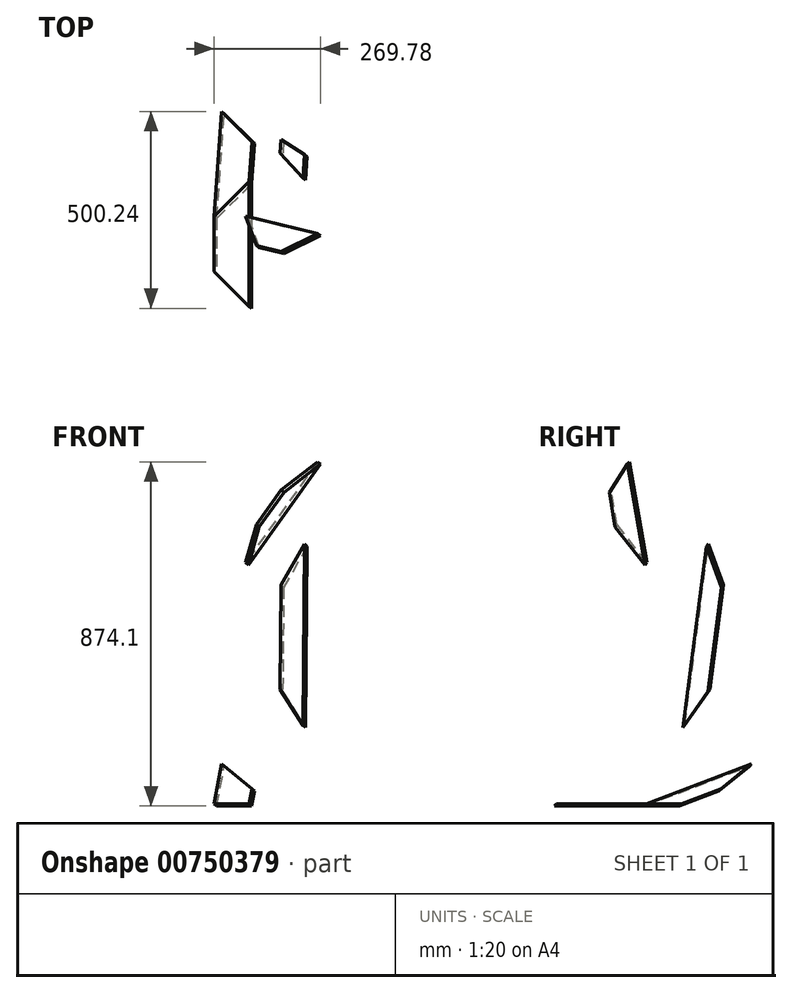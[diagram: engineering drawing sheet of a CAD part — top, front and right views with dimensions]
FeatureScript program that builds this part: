
annotation { "Feature Type Name" : "Feature", "Feature Type Description" : "" }
export const myFeature = defineFeature(function(context is Context, id is Id, definition is map)
    precondition{}
    {
        {
            var Q0;
            Q0=qCreatedBy(makeId("Top.planeOp"),FACE);
            var sketch = newSketch(context, id + "F0", { "sketchPlane" : qUnion([Q0])});
            skLineSegment(sketch, "E0", {"start": v(0, -158.75) * mm, "end": v(0, 158.75) * mm, "construction": true});
            skLineSegment(sketch, "E1", {"start": v(-44.45, 158.75) * mm, "end": v(44.45, 158.75) * mm, "construction": true});
            skLineSegment(sketch, "E2", {"start": v(-44.45, 0) * mm, "end": v(44.45, 0) * mm});
            skLineSegment(sketch, "E3", {"start": v(44.45, 0) * mm, "end": v(44.45, 158.75) * mm});
            skLineSegment(sketch, "E4", {"start": v(-44.45, 0) * mm, "end": v(-44.45, 69.85) * mm});
            skLineSegment(sketch, "E5", {"start": v(-44.45, 69.85) * mm, "end": v(44.45, 158.75) * mm});
            skLineSegment(sketch, "E6.MirrorCS", {"start": v(-44.45, 0) * mm, "end": v(-44.45, -69.85) * mm});
            skLineSegment(sketch, "E7.MirrorCS", {"start": v(-44.45, -69.85) * mm, "end": v(44.45, -158.75) * mm});
            skLineSegment(sketch, "E8.MirrorCS", {"start": v(44.45, 0) * mm, "end": v(44.45, -158.75) * mm});
            skLineSegment(sketch, "E9", {"start": v(44.45, 69.85) * mm, "end": v(-77.04, 191.34) * mm, "construction": true});
            skPoint(sketch, "E10", {"position": v(0, 114.3) * mm});
            skLineSegment(sketch, "E11.MirrorCS", {"start": v(44.45, -69.85) * mm, "end": v(-77.04, -191.34) * mm, "construction": true});
            skPoint(sketch, "E12.MirrorP", {"position": v(0, -114.3) * mm});
            skSolve(sketch);
        }
        {
            var Q0;
            Q0=sQuery(id+"F0.wireOp",VERTEX,"E10");
            var Q1;
            Q1=sQuery(id+"F0.wireOp",EDGE,"E5");
            cPlane(context, id + "F1", {"entities" : qUnion([Q0, Q1]), "cplaneType" : CPlaneType.LINE_POINT, "offset" : 25.4 * mm, "width" : 152.4 * mm, "height" : 152.4 * mm});
        }
        {
            assignVariable(context, id + "F2", {"name" : "al", "anyValue" : 30});
        }
        {
            var Q0;
            Q0=qCreatedBy(id+"F1.planeOp",FACE);
            var sketch = newSketch(context, id + "F3", { "sketchPlane" : qUnion([Q0])});
            skLineSegment(sketch, "E13", {"start": v(80.82, 0) * mm, "end": v(313.77, 134.5) * mm, "construction": true});
            skLineSegment(sketch, "E14", {"start": v(80.82, 0) * mm, "end": v(-55.6, 236.3) * mm, "construction": true});
            skSolve(sketch);
        }
        {
            var Q0;
            Q0=sQuery(id+"F0.wireOp",EDGE,"E5");
            cPoint(context, id + "F4", {"entities" : qUnion([Q0]), "parameter" : 0.5});
        }
        {
            var Q0;
            Q0 = qCreatedBy(id + "F4" ,VERTEX);
            var Q1;
            Q1=sQuery(id+"F3.wireOp",EDGE,"E14");
            cPlane(context, id + "F5", {"entities" : qUnion([Q0, Q1]), "cplaneType" : CPlaneType.LINE_POINT, "offset" : 25.4 * mm, "width" : 152.4 * mm, "height" : 152.4 * mm});
        }
        {
            var Q0;
            Q0=qCreatedBy(id+"F5.planeOp",FACE);
            var sketch = newSketch(context, id + "F6", { "sketchPlane" : qUnion([Q0])});
            skPoint(sketch, "E15", {"position": v(15.27, 105.82) * mm});
            skLineSegment(sketch, "E16", {"start": v(15.27, 105.82) * mm, "end": v(15.87, 114.08) * mm, "construction": true});
            skLineSegment(sketch, "E17", {"start": v(-32.25, 64.67) * mm, "end": v(-11.76, 349.97) * mm});
            skLineSegment(sketch, "E18", {"start": v(70.54, 254.94) * mm, "end": v(62.8, 146.97) * mm});
            skLineSegment(sketch, "E19", {"start": v(62.8, 146.97) * mm, "end": v(-32.25, 64.67) * mm});
            skLineSegment(sketch, "E20", {"start": v(-178.95, 218.59) * mm, "end": v(135.87, 195.99) * mm, "construction": true});
            skPoint(sketch, "E21", {"position": v(-22, 207.32) * mm});
            skLineSegment(sketch, "E22.MirrorCS", {"start": v(70.54, 254.94) * mm, "end": v(-11.76, 349.97) * mm});
            skPoint(sketch, "E23", {"position": v(66.67, 200.95) * mm});
            skLineSegment(sketch, "E24", {"start": v(-18.13, 261.3) * mm, "end": v(108.46, 370.93) * mm, "construction": true});
            skPoint(sketch, "E25", {"position": v(29.4, 302.45) * mm});
            skSolve(sketch);
        }
        {
            var Q0;
            Q0=sQuery(id+"F6.wireOp",VERTEX,"E25");
            var Q1;
            Q1=sQuery(id+"F6.wireOp",EDGE,"E22.MirrorCS");
            cPlane(context, id + "F7", {"entities" : qUnion([Q0, Q1]), "cplaneType" : CPlaneType.LINE_POINT, "offset" : 25.4 * mm, "width" : 152.4 * mm, "height" : 152.4 * mm});
        }
        {
            var Q0;
            Q0=qCreatedBy(id+"F7.planeOp",FACE);
            var sketch = newSketch(context, id + "F8", { "sketchPlane" : qUnion([Q0])});
            skLineSegment(sketch, "E26", {"start": v(-215.04, 62.34) * mm, "end": v(-136.1, 114.46) * mm, "construction": true});
            skLineSegment(sketch, "E27", {"start": v(-215.04, 62.34) * mm, "end": v(-258.43, 128.06) * mm, "construction": true});
            skSolve(sketch);
        }
        {
            var Q0;
            Q0=sQuery(id+"F8.wireOp",EDGE,"E26");
            var Q1;
            Q1=sQuery(id+"F6.wireOp",VERTEX,"E25");
            cPlane(context, id + "F9", {"entities" : qUnion([Q0, Q1]), "cplaneType" : CPlaneType.LINE_POINT, "offset" : 25.4 * mm, "width" : 152.4 * mm, "height" : 152.4 * mm});
        }
        {
            var Q0;
            Q0=qCreatedBy(id+"F9.planeOp",FACE);
            var sketch = newSketch(context, id + "F10", { "sketchPlane" : qUnion([Q0])});
            skLineSegment(sketch, "E28", {"start": v(44.88, 220.3) * mm, "end": v(50.56, 684.58) * mm});
            skLineSegment(sketch, "E29", {"start": v(50.56, 684.58) * mm, "end": v(-28.92, 587.17) * mm});
            skLineSegment(sketch, "E30", {"start": v(-28.92, 587.17) * mm, "end": v(-32.2, 319.62) * mm});
            skLineSegment(sketch, "E31", {"start": v(-32.2, 319.62) * mm, "end": v(44.88, 220.3) * mm});
            skLineSegment(sketch, "E32", {"start": v(-30.56, 453.4) * mm, "end": v(47.72, 452.44) * mm, "construction": true});
            skPoint(sketch, "E33", {"position": v(10.82, 635.87) * mm});
            skLineSegment(sketch, "E34", {"start": v(10.82, 635.87) * mm, "end": v(-66.7, 699.11) * mm, "construction": true});
            skSolve(sketch);
        }
        {
            var Q0;
            Q0=sQuery(id+"F10.wireOp",EDGE,"E29");
            cPlane(context, id + "F11", {"entities" : qUnion([Q0]), "cplaneType" : CPlaneType.LINE_ANGLE, "offset" : 25.4 * mm, "angle" : (getVariable(context, 'al')) * degree, "width" : 152.4 * mm, "height" : 152.4 * mm});
        }
        {
            var Q0;
            Q0=qCreatedBy(id+"F11.planeOp",FACE);
            var sketch = newSketch(context, id + "F12", { "sketchPlane" : qUnion([Q0])});
            skLineSegment(sketch, "E35", {"start": v(197.52, 584.55) * mm, "end": v(214.81, 691.72) * mm});
            skLineSegment(sketch, "E36", {"start": v(214.81, 691.72) * mm, "end": v(162.4, 806) * mm});
            skLineSegment(sketch, "E37", {"start": v(162.4, 806) * mm, "end": v(111.84, 492.55) * mm});
            skLineSegment(sketch, "E38", {"start": v(111.84, 492.55) * mm, "end": v(197.52, 584.55) * mm});
            skLineSegment(sketch, "E39", {"start": v(206.17, 638.13) * mm, "end": v(137.11, 649.27) * mm});
            skSolve(sketch);
        }
        {
            var Q0;
            {var subQ0=sQuery(id+"F12.wireOp",EDGE,"E38");Q0=makeQuery(id+"F12.imprint","IMPRINT",FACE,{"disambiguationData":[TD([[makeQuery(id+"F12.imprint","IMPRINT",EDGE,{"derivedFrom":subQ0}),1.0]])]});}
            var Q1;
            Q1=makeQuery(id+"F6.imprint","IMPRINT",FACE,{"disambiguationData":[TD([[makeQuery(id+"F6.imprint","IMPRINT",EDGE,{"derivedFrom":sQuery(id+"F6.wireOp",EDGE,"E17")}),-1.0]])]});
            var Q2;
            Q2=makeQuery(id+"F10.imprint","IMPRINT",FACE,{"disambiguationData":[TD([[makeQuery(id+"F10.imprint","IMPRINT",EDGE,{"derivedFrom":sQuery(id+"F10.wireOp",EDGE,"E28")}),1.0]])]});
            var Q3;
            {var subQ0=sQuery(id+"F12.wireOp",EDGE,"E36");Q3=makeQuery(id+"F12.imprint","IMPRINT",FACE,{"disambiguationData":[TD([[makeQuery(id+"F12.imprint","IMPRINT",EDGE,{"derivedFrom":subQ0}),1.0]])]});}
            var Q4;
            Q4=makeQuery(id+"F0.imprint","IMPRINT",FACE,{"disambiguationData":[TD([[makeQuery(id+"F0.imprint","IMPRINT",EDGE,{"derivedFrom":sQuery(id+"F0.wireOp",EDGE,"E2")}),-1.0]])]});
            var Q5;
            Q5=makeQuery(id+"F0.imprint","IMPRINT",FACE,{"disambiguationData":[TD([[makeQuery(id+"F0.imprint","IMPRINT",EDGE,{"derivedFrom":sQuery(id+"F0.wireOp",EDGE,"E2")}),1.0]])]});
            extrude(context, id + "F13", {"entities" : qUnion([Q0, Q1, Q2, Q3, Q4, Q5]), "depth" : 10 * mm, "offsetDistance" : 25.4 * mm});
        }
    });
